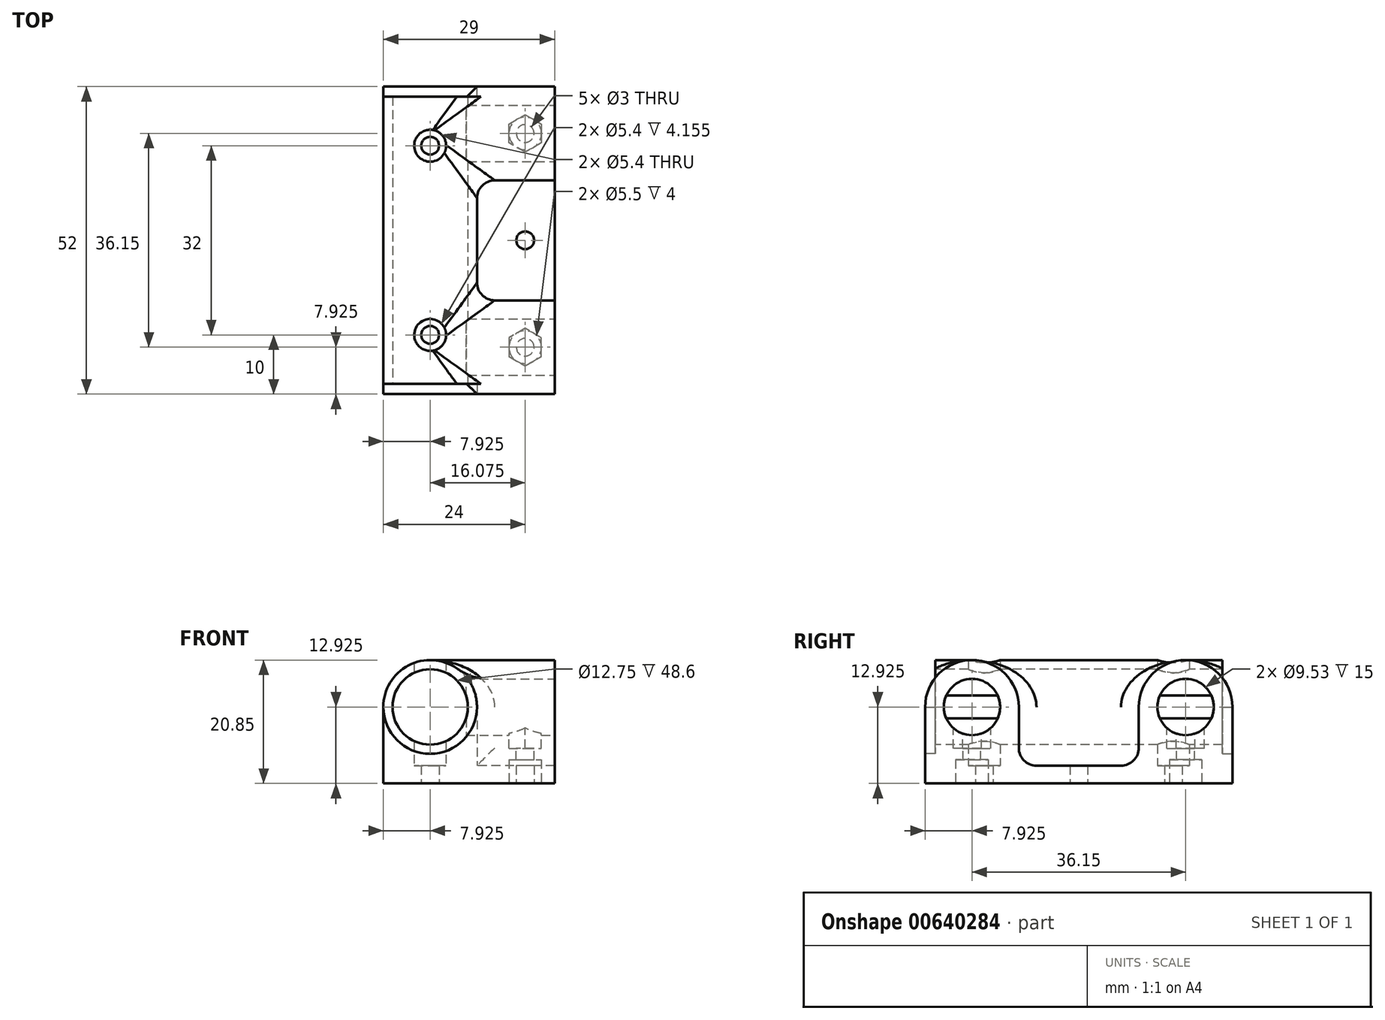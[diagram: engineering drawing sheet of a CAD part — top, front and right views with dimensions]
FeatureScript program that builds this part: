
annotation { "Feature Type Name" : "Feature", "Feature Type Description" : "" }
export const myFeature = defineFeature(function(context is Context, id is Id, definition is map)
    precondition{}
    {
        {
            var Q0;
            Q0=qCreatedBy(makeId("Front.planeOp"),FACE);
            var sketch = newSketch(context, id + "F0", { "sketchPlane" : qUnion([Q0])});
            skLineSegment(sketch, "E0", {"start": v(0, 0) * mm, "end": v(15.85, 0) * mm});
            skLineSegment(sketch, "E1", {"start": v(7.92, 0) * mm, "end": v(7.92, 12.92) * mm, "construction": true});
            skCircle(sketch, "E2", {"center": v(7.92, 12.92) * mm, "radius": 7.92 * mm});
            skLineSegment(sketch, "E3", {"start": v(0, 0) * mm, "end": v(0, 12.92) * mm});
            skLineSegment(sketch, "E4", {"start": v(15.85, 0) * mm, "end": v(15.85, 12.92) * mm});
            skSolve(sketch);
        }
        {
            var Q0;
            Q0 = qSketchRegion(id + "F0", true);
            extrude(context, id + "F1", {"entities" : qUnion([Q0]), "depth" : 52 * mm, "offsetDistance" : 25 * mm});
        }
        {
            var Q0;
            Q0=makeQuery(id+"F1.opExtrude","SWEPT_FACE",FACE,{"disambiguationData":[OSD([sQuery(id+"F0.wireOp",EDGE,"E4")])]});
            var sketch = newSketch(context, id + "F2", { "sketchPlane" : qUnion([Q0])});
            skLineSegment(sketch, "E5.0", {"start": v(-52, 0) * mm, "end": v(0, 0) * mm});
            skLineSegment(sketch, "E6.0", {"start": v(-52, 0) * mm, "end": v(-52, 12.92) * mm});
            skLineSegment(sketch, "E6.1", {"start": v(0, 0) * mm, "end": v(0, 12.92) * mm});
            skLineSegment(sketch, "E7", {"start": v(-52, 12.92) * mm, "end": v(-36.15, 12.92) * mm, "construction": true});
            skCircle(sketch, "E8", {"center": v(-44.08, 12.92) * mm, "radius": 7.93 * mm});
            skLineSegment(sketch, "E9", {"start": v(-26, 0) * mm, "end": v(-26, 12.92) * mm, "construction": true});
            skCircle(sketch, "E10.MirrorC", {"center": v(-7.93, 12.92) * mm, "radius": 7.93 * mm});
            skLineSegment(sketch, "E11", {"start": v(-36.15, 12.92) * mm, "end": v(-36.15, 0) * mm});
            skLineSegment(sketch, "E12", {"start": v(-36.15, 0) * mm, "end": v(-36.15, 3) * mm});
            skLineSegment(sketch, "E13", {"start": v(-36.15, 3) * mm, "end": v(-15.85, 3) * mm});
            skLineSegment(sketch, "E14", {"start": v(-15.85, 12.92) * mm, "end": v(-15.85, 3) * mm});
            skSolve(sketch);
        }
        {
            var Q0;
            Q0 = qSketchRegion(id + "F2", true);
            extrude(context, id + "F3", {"entities" : qUnion([Q0]), "operationType" : NewBodyOperationType.ADD, "depth" : (26 - 12.85) * mm, "offsetDistance" : 25 * mm, "hasSecondDirection" : true, "secondDirectionOppositeDirection" : true, "secondDirectionDepth" : (15.85 / 2) * mm});
        }
        {
            var Q0;
            Q0=makeQuery(id+"F3.boolean.opBoolean","MERGE",FACE,{"derivedFrom":[makeQuery(id+"F1.opExtrude","CAP_FACE",FACE,{"disambiguationData":[OSD([sQuery(id+"F0.wireOp",EDGE,"E0"),sQuery(id+"F0.wireOp",EDGE,"E2"),sQuery(id+"F0.wireOp",EDGE,"E3"),sQuery(id+"F0.wireOp",EDGE,"E4")])],"isStart":false}),makeQuery(id+"F3.opExtrude","SWEPT_FACE",FACE,{"disambiguationData":[OSD([sQuery(id+"F2.wireOp",EDGE,"E6.0")])]})]});
            var sketch = newSketch(context, id + "F4", { "sketchPlane" : qUnion([Q0])});
            skArc(sketch, "E15.0", {"start": v(15.85, 12.92) * mm, "mid": v(7.92, 20.85) * mm, "end": v(0, 12.93) * mm, "construction": true});
            skCircle(sketch, "E16", {"center": v(7.92, 12.92) * mm, "radius": 6.38 * mm});
            skSolve(sketch);
        }
        {
            var Q0;
            Q0 = qSketchRegion(id + "F4", true);
            extrude(context, id + "F5", {"entities" : qUnion([Q0]), "operationType" : NewBodyOperationType.REMOVE, "oppositeDirection" : true, "depth" : 100 * mm, "offsetDistance" : 25 * mm});
        }
        {
            var Q0;
            Q0=makeQuery(id+"F3.opExtrude","CAP_FACE",FACE,{"disambiguationData":[OSD([sQuery(id+"F2.wireOp",EDGE,"E5.0"),sQuery(id+"F2.wireOp",EDGE,"E6.0"),sQuery(id+"F2.wireOp",EDGE,"E6.1"),sQuery(id+"F2.wireOp",EDGE,"E8"),sQuery(id+"F2.wireOp",EDGE,"E10.MirrorC"),sQuery(id+"F2.wireOp",EDGE,"eMA8j27x-38BE-MHN1-lJ3s-BBI1wRVpQBKV")])],"isStart":false});
            var sketch = newSketch(context, id + "F6", { "sketchPlane" : qUnion([Q0])});
            skLineSegment(sketch, "E17.0", {"start": v(-52, 12.93) * mm, "end": v(-52, 12.93) * mm});
            skLineSegment(sketch, "E17.1", {"start": v(0, 12.93) * mm, "end": v(0, 12.93) * mm});
            skCircle(sketch, "E18", {"center": v(-44.08, 12.92) * mm, "radius": 4.76 * mm});
            skCircle(sketch, "E19", {"center": v(-7.93, 12.92) * mm, "radius": 4.76 * mm});
            skSolve(sketch);
        }
        {
            var Q0;
            Q0 = qSketchRegion(id + "F6", true);
            extrude(context, id + "F7", {"entities" : qUnion([Q0]), "operationType" : NewBodyOperationType.REMOVE, "oppositeDirection" : true, "depth" : 15 * mm, "offsetDistance" : 25 * mm});
        }
        {
            var Q0;
            Q0=makeQuery(id+"F3.boolean.opBoolean","MERGE",FACE,{"derivedFrom":[makeQuery(id+"F1.opExtrude","CAP_FACE",FACE,{"disambiguationData":[OSD([sQuery(id+"F0.wireOp",EDGE,"E0"),sQuery(id+"F0.wireOp",EDGE,"E2"),sQuery(id+"F0.wireOp",EDGE,"E3"),sQuery(id+"F0.wireOp",EDGE,"E4")])],"isStart":false}),makeQuery(id+"F3.opExtrude","SWEPT_FACE",FACE,{"disambiguationData":[OSD([sQuery(id+"F2.wireOp",EDGE,"E6.0")])]})]});
            var sketch = newSketch(context, id + "F8", { "sketchPlane" : qUnion([Q0])});
            skCircle(sketch, "E20.0", {"center": v(7.92, 12.92) * mm, "radius": 6.38 * mm});
            skCircle(sketch, "E21", {"center": v(7.92, 12.92) * mm, "radius": 7.92 * mm});
            skSolve(sketch);
        }
        {
            var Q0;
            Q0 = qSketchRegion(id + "F8", true);
            extrude(context, id + "F9", {"entities" : qUnion([Q0]), "operationType" : NewBodyOperationType.REMOVE, "oppositeDirection" : true, "depth" : 1.7 * mm, "offsetDistance" : 25 * mm});
        }
        {
            var Q0;
            Q0=makeQuery(id+"F3.boolean.opBoolean","MERGE",FACE,{"derivedFrom":[makeQuery(id+"F1.opExtrude","CAP_FACE",FACE,{"disambiguationData":[OSD([sQuery(id+"F0.wireOp",EDGE,"E0"),sQuery(id+"F0.wireOp",EDGE,"E2"),sQuery(id+"F0.wireOp",EDGE,"E3"),sQuery(id+"F0.wireOp",EDGE,"E4")])],"isStart":true}),makeQuery(id+"F3.opExtrude","SWEPT_FACE",FACE,{"disambiguationData":[OSD([sQuery(id+"F2.wireOp",EDGE,"E6.1")])]})]});
            var sketch = newSketch(context, id + "F10", { "sketchPlane" : qUnion([Q0])});
            skCircle(sketch, "E22.0", {"center": v(-7.92, 12.92) * mm, "radius": 6.38 * mm});
            skCircle(sketch, "E23", {"center": v(-7.92, 12.92) * mm, "radius": 7.92 * mm});
            skSolve(sketch);
        }
        {
            var Q0;
            Q0 = qSketchRegion(id + "F10", true);
            extrude(context, id + "F11", {"entities" : qUnion([Q0]), "operationType" : NewBodyOperationType.REMOVE, "oppositeDirection" : true, "depth" : 1.7 * mm, "offsetDistance" : 25 * mm});
        }
        {
            var Q0;
            Q0=qCreatedBy(makeId("Top.planeOp"),FACE);
            var sketch = newSketch(context, id + "F12", { "sketchPlane" : qUnion([Q0])});
            skPoint(sketch, "E24.0", {"position": v(0, -52) * mm});
            skPoint(sketch, "E24.1", {"position": v(29, 0) * mm});
            skLineSegment(sketch, "E25.bottom", {"start": v(29, 0) * mm, "end": v(0, 0) * mm, "construction": true});
            skLineSegment(sketch, "E25.top", {"start": v(29, -52) * mm, "end": v(0, -52) * mm, "construction": true});
            skLineSegment(sketch, "E25.left", {"start": v(29, 0) * mm, "end": v(29, -52) * mm, "construction": true});
            skLineSegment(sketch, "E25.right", {"start": v(0, 0) * mm, "end": v(0, -52) * mm, "construction": true});
            skLineSegment(sketch, "E26", {"start": v(14.5, -52) * mm, "end": v(14.5, -42) * mm, "construction": true});
            skPoint(sketch, "E26.endSnap0", {"position": v(14.5, -52) * mm});
            skCircle(sketch, "E27", {"center": v(24, -42) * mm, "radius": 1.5 * mm, "construction": true});
            skCircle(sketch, "E28", {"center": v(7.92, -42) * mm, "radius": 1.5 * mm});
            skLineSegment(sketch, "E29", {"start": v(0, -26) * mm, "end": v(13.04, -26) * mm, "construction": true});
            skCircle(sketch, "E30.MirrorC", {"center": v(7.92, -10) * mm, "radius": 1.5 * mm});
            skCircle(sketch, "E31.MirrorC", {"center": v(24, -10) * mm, "radius": 1.5 * mm, "construction": true});
            skLineSegment(sketch, "E32", {"start": v(24, -42) * mm, "end": v(24, -10) * mm, "construction": true});
            skCircle(sketch, "E33", {"center": v(24, -26) * mm, "radius": 1.5 * mm});
            skLineSegment(sketch, "E34", {"start": v(7.92, -42) * mm, "end": v(0, -42) * mm, "construction": true});
            skLineSegment(sketch, "E35", {"start": v(24, -42) * mm, "end": v(29, -42) * mm, "construction": true});
            skSolve(sketch);
        }
        {
            var Q0;
            Q0 = qSketchRegion(id + "F12", true);
            extrude(context, id + "F13", {"entities" : qUnion([Q0]), "operationType" : NewBodyOperationType.REMOVE, "depth" : 25 * mm, "offsetDistance" : 25 * mm});
        }
        {
            var Q0;
            Q0=qCreatedBy(makeId("Top.planeOp"),FACE);
            cPlane(context, id + "F14", {"entities" : qUnion([Q0]), "cplaneType" : CPlaneType.OFFSET, "offset" : 3 * mm, "width" : 150 * mm, "height" : 150 * mm});
        }
        {
            var Q0;
            Q0=qCreatedBy(id+"F14.planeOp",FACE);
            var sketch = newSketch(context, id + "F15", { "sketchPlane" : qUnion([Q0])});
            skArc(sketch, "E36.0", {"start": v(8.74, -8.74) * mm, "mid": v(8.99, -8.94) * mm, "end": v(9.18, -9.18) * mm, "construction": true});
            skArc(sketch, "E36.1", {"start": v(9.18, -9.18) * mm, "mid": v(6.86, -11.06) * mm, "end": v(8.74, -8.74) * mm, "construction": true});
            skCircle(sketch, "E36.2", {"center": v(21, -7.93) * mm, "radius": 1.5 * mm, "construction": true});
            skArc(sketch, "E36.3", {"start": v(8.74, -43.26) * mm, "mid": v(8.99, -43.06) * mm, "end": v(9.18, -42.82) * mm, "construction": true});
            skArc(sketch, "E36.4", {"start": v(8.74, -43.26) * mm, "mid": v(6.86, -40.94) * mm, "end": v(9.18, -42.82) * mm, "construction": true});
            skCircle(sketch, "E36.5", {"center": v(21, -44.08) * mm, "radius": 1.5 * mm, "construction": true});
            skCircle(sketch, "E37", {"center": v(7.92, -42) * mm, "radius": 2.7 * mm});
            skCircle(sketch, "E38", {"center": v(7.92, -10) * mm, "radius": 2.7 * mm});
            skSolve(sketch);
        }
        {
            var Q0;
            Q0 = qSketchRegion(id + "F15", true);
            extrude(context, id + "F16", {"entities" : qUnion([Q0]), "operationType" : NewBodyOperationType.REMOVE, "depth" : 25 * mm, "offsetDistance" : 25 * mm});
        }
        {
            var Q0;
            Q0=makeQuery(id+"F3.boolean.opBoolean","INTERSECT",EDGE,{"derivedFrom":[makeQuery(id+"F1.opExtrude","SWEPT_FACE",FACE,{"disambiguationData":[OSD([sQuery(id+"F0.wireOp",EDGE,"E4")])]}),makeQuery(id+"F3.opExtrude","SWEPT_FACE",FACE,{"disambiguationData":[OSD([sQuery(id+"F2.wireOp",EDGE,"E11")])]})]});
            var Q1;
            Q1=makeQuery(id+"F3.boolean.opBoolean","INTERSECT",EDGE,{"disambiguationData":[OD(1.0)],"derivedFrom":[makeQuery(id+"F1.opExtrude","SWEPT_FACE",FACE,{"disambiguationData":[OSD([sQuery(id+"F0.wireOp",EDGE,"E2")])]}),makeQuery(id+"F3.opExtrude","SWEPT_FACE",FACE,{"disambiguationData":[OSD([sQuery(id+"F2.wireOp",EDGE,"E8")])]})]});
            var Q2;
            Q2=makeQuery(id+"F3.opExtrude","SWEPT_EDGE",EDGE,{"disambiguationData":[OSD([sQuery(id+"F2.wireOp",EDGE,"E11"),sQuery(id+"F2.wireOp",EDGE,"E12"),sQuery(id+"F2.wireOp",EDGE,"E13")])]});
            var Q3;
            Q3=makeQuery(id+"F3.opExtrude","SWEPT_EDGE",EDGE,{"disambiguationData":[OSD([sQuery(id+"F2.wireOp",EDGE,"E13"),sQuery(id+"F2.wireOp",EDGE,"E14")])]});
            var Q4;
            Q4=makeQuery(id+"F3.boolean.opBoolean","INTERSECT",EDGE,{"derivedFrom":[makeQuery(id+"F1.opExtrude","SWEPT_FACE",FACE,{"disambiguationData":[OSD([sQuery(id+"F0.wireOp",EDGE,"E4")])]}),makeQuery(id+"F3.opExtrude","SWEPT_FACE",FACE,{"disambiguationData":[OSD([sQuery(id+"F2.wireOp",EDGE,"E14")])]})]});
            var Q5;
            Q5=makeQuery(id+"F3.boolean.opBoolean","INTERSECT",EDGE,{"disambiguationData":[OD(1.0)],"derivedFrom":[makeQuery(id+"F1.opExtrude","SWEPT_FACE",FACE,{"disambiguationData":[OSD([sQuery(id+"F0.wireOp",EDGE,"E2")])]}),makeQuery(id+"F3.opExtrude","SWEPT_FACE",FACE,{"disambiguationData":[OSD([sQuery(id+"F2.wireOp",EDGE,"E10.MirrorC")])]})]});
            var Q6;
            {var subQ0=makeQuery(id+"F1.opExtrude","SWEPT_FACE",FACE,{"disambiguationData":[OSD([sQuery(id+"F0.wireOp",EDGE,"E2")])]});var subQ1=makeQuery(id+"F3.opExtrude","SWEPT_FACE",FACE,{"disambiguationData":[OSD([sQuery(id+"F2.wireOp",EDGE,"E8")])]});Q6=makeQuery(id+"F9.boolean.opBoolean","SPLIT",EDGE,{"disambiguationData":[topologyDisambiguationEdgeConnected([subQ0])],"derivedFrom":makeQuery(id+"F3.boolean.opBoolean","INTERSECT",EDGE,{"disambiguationData":[OD(0.0)],"derivedFrom":[subQ0,subQ1]})});}
            var Q7;
            {var subQ0=makeQuery(id+"F1.opExtrude","SWEPT_FACE",FACE,{"disambiguationData":[OSD([sQuery(id+"F0.wireOp",EDGE,"E2")])]});var subQ1=makeQuery(id+"F3.opExtrude","SWEPT_FACE",FACE,{"disambiguationData":[OSD([sQuery(id+"F2.wireOp",EDGE,"E10.MirrorC")])]});Q7=makeQuery(id+"F11.boolean.opBoolean","SPLIT",EDGE,{"disambiguationData":[topologyDisambiguationEdgeConnected([subQ0])],"derivedFrom":makeQuery(id+"F3.boolean.opBoolean","INTERSECT",EDGE,{"disambiguationData":[OD(0.0)],"derivedFrom":[subQ0,subQ1]})});}
            fillet(context, id + "F17", {"entities" : qUnion([Q0, Q1, Q2, Q3, Q4, Q5, Q6, Q7]), "radius" : 3 * mm, "tangentPropagation" : true, "allowEdgeOverflow" : false});
        }
        {
            var Q0;
            Q0=qCreatedBy(makeId("Top.planeOp"),FACE);
            cPlane(context, id + "F18", {"entities" : qUnion([Q0]), "cplaneType" : CPlaneType.OFFSET, "offset" : 12.93 * mm, "width" : 150 * mm, "height" : 150 * mm});
        }
        {
            var Q0;
            Q0=qCreatedBy(id+"F18.planeOp",FACE);
            var sketch = newSketch(context, id + "F19", { "sketchPlane" : qUnion([Q0])});
            skPoint(sketch, "E39.0", {"position": v(29, -7.93) * mm});
            skPoint(sketch, "E39.1", {"position": v(29, -44.08) * mm});
            skLineSegment(sketch, "E40", {"start": v(29, -7.93) * mm, "end": v(24, -7.93) * mm, "construction": true});
            skCircle(sketch, "E41.cCircle", {"center": v(24, -7.93) * mm, "radius": 2.75 * mm, "construction": true});
            skLineSegment(sketch, "E41.0", {"start": v(26.75, -6.34) * mm, "end": v(26.75, -9.51) * mm});
            skLineSegment(sketch, "E41.1", {"start": v(26.75, -9.51) * mm, "end": v(24, -11.1) * mm});
            skLineSegment(sketch, "E41.2", {"start": v(24, -11.1) * mm, "end": v(21.25, -9.51) * mm});
            skLineSegment(sketch, "E41.3", {"start": v(21.25, -9.51) * mm, "end": v(21.25, -6.34) * mm});
            skLineSegment(sketch, "E41.4", {"start": v(21.25, -6.34) * mm, "end": v(24, -4.75) * mm});
            skLineSegment(sketch, "E41.5", {"start": v(24, -4.75) * mm, "end": v(26.75, -6.34) * mm});
            skPoint(sketch, "E41.0.midPoint", {"position": v(26.75, -7.93) * mm});
            skPoint(sketch, "E42.0", {"position": v(29, -26) * mm});
            skLineSegment(sketch, "E43", {"start": v(29, -26) * mm, "end": v(17.5, -26) * mm, "construction": true});
            skLineSegment(sketch, "E44.MirrorCS", {"start": v(24, -47.25) * mm, "end": v(26.75, -45.66) * mm});
            skLineSegment(sketch, "E45.MirrorCS", {"start": v(21.25, -45.66) * mm, "end": v(24, -47.25) * mm});
            skLineSegment(sketch, "E46.MirrorCS", {"start": v(21.25, -42.49) * mm, "end": v(21.25, -45.66) * mm});
            skLineSegment(sketch, "E47.MirrorCS", {"start": v(24, -40.9) * mm, "end": v(21.25, -42.49) * mm});
            skLineSegment(sketch, "E48.MirrorCS", {"start": v(26.75, -42.49) * mm, "end": v(24, -40.9) * mm});
            skLineSegment(sketch, "E49.MirrorCS", {"start": v(26.75, -45.66) * mm, "end": v(26.75, -42.49) * mm});
            skSolve(sketch);
        }
        {
            var Q0;
            Q0 = qSketchRegion(id + "F19", true);
            extrude(context, id + "F20", {"entities" : qUnion([Q0]), "operationType" : NewBodyOperationType.REMOVE, "oppositeDirection" : true, "depth" : 7 * mm, "offsetDistance" : 25 * mm});
        }
        {
            var Q0;
            Q0=makeQuery(id+"F20.boolean.opBoolean","COPY",FACE,{"derivedFrom":makeQuery(id+"F20.opExtrude","CAP_FACE",FACE,{"disambiguationData":[OSD([sQuery(id+"F19.wireOp",EDGE,"E41.0"),sQuery(id+"F19.wireOp",EDGE,"E41.1"),sQuery(id+"F19.wireOp",EDGE,"E41.2"),sQuery(id+"F19.wireOp",EDGE,"E41.3"),sQuery(id+"F19.wireOp",EDGE,"E41.4"),sQuery(id+"F19.wireOp",EDGE,"E41.5")])],"isStart":false})});
            var sketch = newSketch(context, id + "F21", { "sketchPlane" : qUnion([Q0])});
            skPoint(sketch, "E50.0", {"position": v(24, -4.75) * mm});
            skPoint(sketch, "E50.1", {"position": v(24, -11.1) * mm});
            skLineSegment(sketch, "E51", {"start": v(24, -4.75) * mm, "end": v(24, -11.1) * mm, "construction": true});
            skCircle(sketch, "E52", {"center": v(24, -7.93) * mm, "radius": 1.5 * mm});
            skPoint(sketch, "E53.0", {"position": v(29, -26) * mm});
            skLineSegment(sketch, "E54", {"start": v(29, -26) * mm, "end": v(24.33, -26) * mm, "construction": true});
            skCircle(sketch, "E55.MirrorC", {"center": v(24, -44.08) * mm, "radius": 1.5 * mm});
            skSolve(sketch);
        }
        {
            var Q0;
            Q0 = qSketchRegion(id + "F21", true);
            extrude(context, id + "F22", {"entities" : qUnion([Q0]), "operationType" : NewBodyOperationType.REMOVE, "oppositeDirection" : true, "depth" : 25 * mm, "offsetDistance" : 25 * mm});
        }
        {
            var Q0;
            Q0=makeQuery(id+"F3.boolean.opBoolean","MERGE",FACE,{"derivedFrom":[makeQuery(id+"F1.opExtrude","SWEPT_FACE",FACE,{"disambiguationData":[OSD([sQuery(id+"F0.wireOp",EDGE,"E0")])]}),makeQuery(id+"F3.opExtrude","SWEPT_FACE",FACE,{"disambiguationData":[OSD([sQuery(id+"F2.wireOp",EDGE,"E5.0")])]})]});
            var sketch = newSketch(context, id + "F23", { "sketchPlane" : qUnion([Q0])});
            skCircle(sketch, "E56", {"center": v(24, 44.08) * mm, "radius": 2.75 * mm});
            skCircle(sketch, "E57", {"center": v(24, 7.93) * mm, "radius": 2.75 * mm});
            skSolve(sketch);
        }
        {
            var Q0;
            Q0 = qSketchRegion(id + "F23", true);
            extrude(context, id + "F24", {"entities" : qUnion([Q0]), "operationType" : NewBodyOperationType.REMOVE, "oppositeDirection" : true, "depth" : 4 * mm, "offsetDistance" : 25 * mm});
        }
    });
